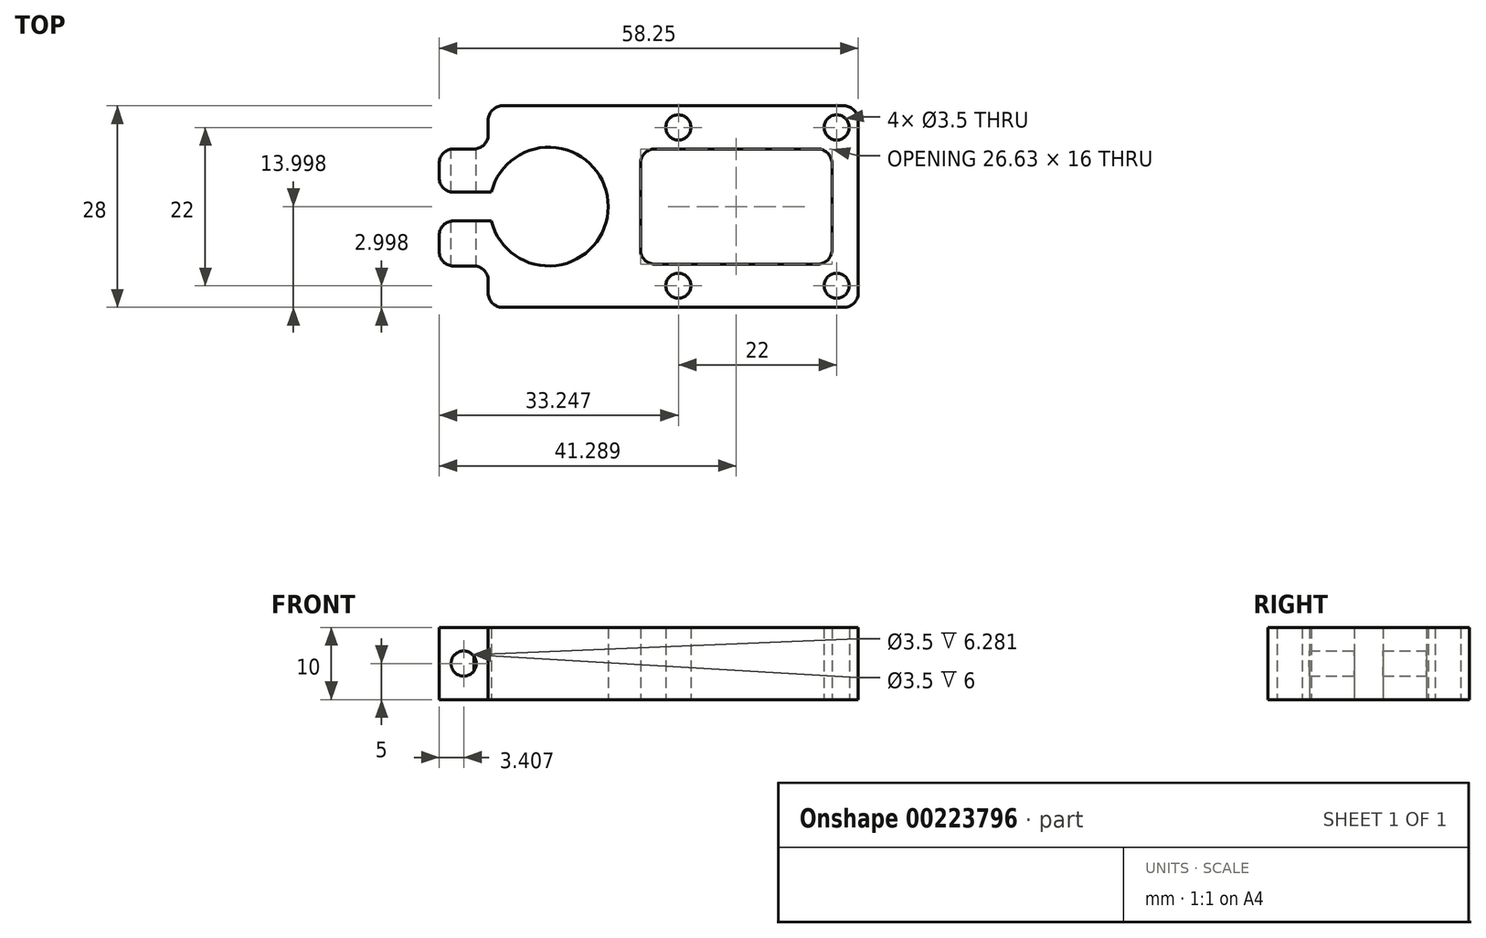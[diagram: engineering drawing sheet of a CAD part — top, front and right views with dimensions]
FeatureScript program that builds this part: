
annotation { "Feature Type Name" : "Feature", "Feature Type Description" : "" }
export const myFeature = defineFeature(function(context is Context, id is Id, definition is map)
    precondition{}
    {
        {
            var Q0;
            Q0=qCreatedBy(makeId("Top.planeOp"),FACE);
            var sketch = newSketch(context, id + "F0", { "sketchPlane" : qUnion([Q0])});
            skArc(sketch, "E0", {"start": v(-51.53, 38.64) * mm, "mid": v(-35.27, 40.64) * mm, "end": v(-51.53, 42.64) * mm});
            skCircle(sketch, "E1", {"center": v(-25.52, 51.64) * mm, "radius": 1.75 * mm});
            skCircle(sketch, "E2", {"center": v(-3.52, 51.64) * mm, "radius": 1.75 * mm});
            skCircle(sketch, "E3", {"center": v(-25.52, 29.64) * mm, "radius": 1.75 * mm});
            skCircle(sketch, "E4", {"center": v(-3.52, 29.64) * mm, "radius": 1.75 * mm});
            skLineSegment(sketch, "E5.bottom", {"start": v(-2.52, 54.64) * mm, "end": v(-49.96, 54.64) * mm});
            skLineSegment(sketch, "E5.top", {"start": v(-2.52, 26.64) * mm, "end": v(-49.96, 26.64) * mm});
            skLineSegment(sketch, "E5.left", {"start": v(-0.52, 52.64) * mm, "end": v(-0.52, 28.64) * mm});
            skLineSegment(sketch, "E5.right", {"start": v(-58.77, 46.64) * mm, "end": v(-58.77, 44.64) * mm});
            skPoint(sketch, "E6.visualSharp", {"position": v(-0.52, 54.64) * mm});
            skArc(sketch, "E6.filletArc", {"start": v(-0.52, 52.64) * mm, "mid": v(-1.1, 54.05) * mm, "end": v(-2.52, 54.64) * mm});
            skPoint(sketch, "E7.visualSharp", {"position": v(-0.52, 26.64) * mm});
            skArc(sketch, "E7.filletArc", {"start": v(-2.52, 26.64) * mm, "mid": v(-1.1, 27.22) * mm, "end": v(-0.52, 28.64) * mm});
            skLineSegment(sketch, "E8", {"start": v(-51.96, 52.64) * mm, "end": v(-51.96, 50.64) * mm});
            skLineSegment(sketch, "E9", {"start": v(-53.96, 48.64) * mm, "end": v(-56.77, 48.64) * mm});
            skLineSegment(sketch, "E10", {"start": v(-51.96, 28.64) * mm, "end": v(-51.96, 30.39) * mm});
            skLineSegment(sketch, "E11", {"start": v(-53.96, 32.39) * mm, "end": v(-56.77, 32.39) * mm});
            skLineSegment(sketch, "E12", {"start": v(-56.77, 42.64) * mm, "end": v(-51.53, 42.64) * mm});
            skLineSegment(sketch, "E13", {"start": v(-56.77, 38.64) * mm, "end": v(-51.53, 38.64) * mm});
            skLineSegment(sketch, "E14.trimOffspring", {"start": v(-58.77, 36.64) * mm, "end": v(-58.77, 34.39) * mm});
            skPoint(sketch, "E15.visualSharp", {"position": v(-51.96, 48.64) * mm});
            skArc(sketch, "E15.filletArc", {"start": v(-53.96, 48.64) * mm, "mid": v(-52.55, 49.22) * mm, "end": v(-51.96, 50.64) * mm});
            skPoint(sketch, "E16.visualSharp", {"position": v(-51.96, 54.64) * mm});
            skArc(sketch, "E16.filletArc", {"start": v(-49.96, 54.64) * mm, "mid": v(-51.38, 54.05) * mm, "end": v(-51.96, 52.64) * mm});
            skPoint(sketch, "E17.visualSharp", {"position": v(-58.77, 48.64) * mm});
            skArc(sketch, "E17.filletArc", {"start": v(-56.77, 48.64) * mm, "mid": v(-58.19, 48.05) * mm, "end": v(-58.77, 46.64) * mm});
            skPoint(sketch, "E18.visualSharp", {"position": v(-58.77, 42.64) * mm});
            skArc(sketch, "E18.filletArc", {"start": v(-58.77, 44.64) * mm, "mid": v(-58.19, 43.22) * mm, "end": v(-56.77, 42.64) * mm});
            skPoint(sketch, "E19.visualSharp", {"position": v(-58.77, 38.64) * mm});
            skArc(sketch, "E19.filletArc", {"start": v(-56.77, 38.64) * mm, "mid": v(-58.19, 38.05) * mm, "end": v(-58.77, 36.64) * mm});
            skPoint(sketch, "E20.visualSharp", {"position": v(-58.77, 32.39) * mm});
            skArc(sketch, "E20.filletArc", {"start": v(-58.77, 34.39) * mm, "mid": v(-58.19, 32.97) * mm, "end": v(-56.77, 32.39) * mm});
            skPoint(sketch, "E21.visualSharp", {"position": v(-51.96, 32.39) * mm});
            skArc(sketch, "E21.filletArc", {"start": v(-51.96, 30.39) * mm, "mid": v(-52.55, 31.8) * mm, "end": v(-53.96, 32.39) * mm});
            skPoint(sketch, "E22.visualSharp", {"position": v(-51.96, 26.64) * mm});
            skArc(sketch, "E22.filletArc", {"start": v(-51.96, 28.64) * mm, "mid": v(-51.38, 27.22) * mm, "end": v(-49.96, 26.64) * mm});
            skLineSegment(sketch, "E23.bottom", {"start": v(-28.8, 48.64) * mm, "end": v(-6.17, 48.64) * mm});
            skLineSegment(sketch, "E23.top", {"start": v(-28.8, 32.64) * mm, "end": v(-6.17, 32.64) * mm});
            skLineSegment(sketch, "E23.left", {"start": v(-30.8, 46.64) * mm, "end": v(-30.8, 34.64) * mm});
            skLineSegment(sketch, "E23.right", {"start": v(-4.17, 46.64) * mm, "end": v(-4.17, 34.64) * mm});
            skPoint(sketch, "E24.visualSharp", {"position": v(-30.8, 48.64) * mm});
            skArc(sketch, "E24.filletArc", {"start": v(-28.8, 48.64) * mm, "mid": v(-30.2, 48.05) * mm, "end": v(-30.8, 46.64) * mm});
            skPoint(sketch, "E25.visualSharp", {"position": v(-30.8, 32.64) * mm});
            skArc(sketch, "E25.filletArc", {"start": v(-30.8, 34.64) * mm, "mid": v(-30.2, 33.22) * mm, "end": v(-28.8, 32.64) * mm});
            skPoint(sketch, "E26.visualSharp", {"position": v(-4.17, 32.64) * mm});
            skArc(sketch, "E26.filletArc", {"start": v(-6.17, 32.64) * mm, "mid": v(-4.75, 33.22) * mm, "end": v(-4.17, 34.64) * mm});
            skPoint(sketch, "E27.visualSharp", {"position": v(-4.17, 48.64) * mm});
            skArc(sketch, "E27.filletArc", {"start": v(-4.17, 46.64) * mm, "mid": v(-4.75, 48.05) * mm, "end": v(-6.17, 48.64) * mm});
            skSolve(sketch);
        }
        {
            var Q0;
            Q0=makeQuery(id+"F0.imprint","IMPRINT",FACE,{"disambiguationData":[TD([[makeQuery(id+"F0.imprint","IMPRINT",EDGE,{"derivedFrom":sQuery(id+"F0.wireOp",EDGE,"E0")}),-1.0]])]});
            extrude(context, id + "F1", {"entities" : qUnion([Q0]), "depth" : 10 * mm});
        }
        {
            var Q0;
            Q0=makeQuery(id+"F1.opExtrude","SWEPT_FACE",FACE,{"disambiguationData":[OSD([sQuery(id+"F0.wireOp",EDGE,"E9")])]});
            var sketch = newSketch(context, id + "F2", { "sketchPlane" : qUnion([Q0])});
            skCircle(sketch, "E28", {"center": v(55.36, 5) * mm, "radius": 1.75 * mm});
            skSolve(sketch);
        }
        {
            var Q0;
            Q0 = qSketchRegion(id + "F2", true);
            extrude(context, id + "F3", {"entities" : qUnion([Q0]), "operationType" : NewBodyOperationType.REMOVE, "oppositeDirection" : true, "depth" : 25.3 * mm});
        }
    });
